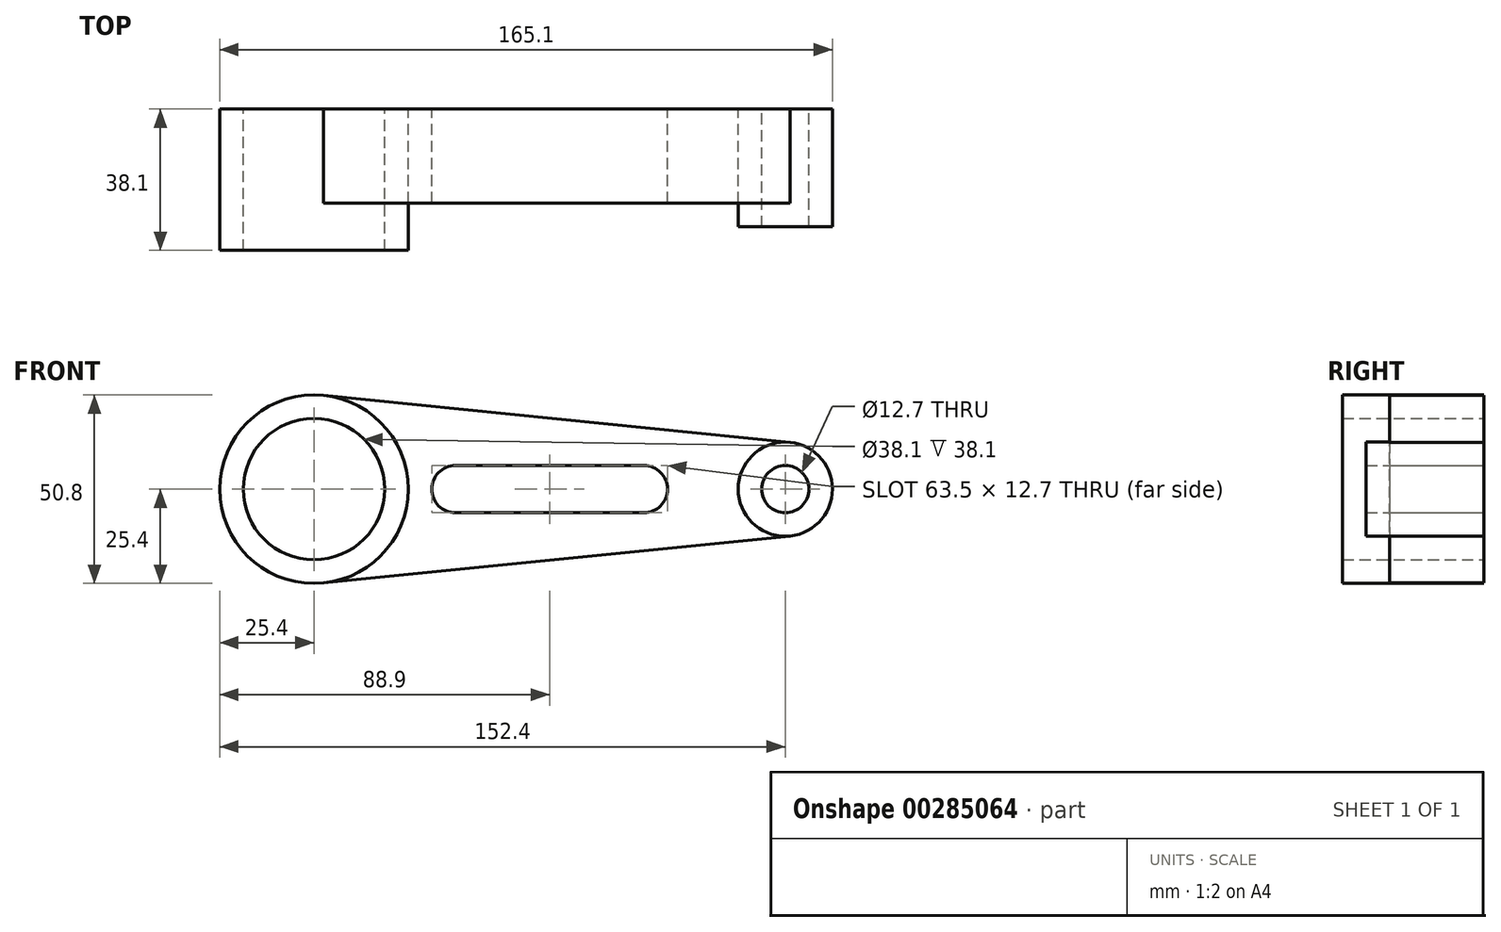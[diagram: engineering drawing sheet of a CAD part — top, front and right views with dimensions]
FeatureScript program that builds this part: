
annotation { "Feature Type Name" : "Feature", "Feature Type Description" : "" }
export const myFeature = defineFeature(function(context is Context, id is Id, definition is map)
    precondition{}
    {
        {
            var Q0;
            Q0=qCreatedBy(makeId("Front.planeOp"),FACE);
            var sketch = newSketch(context, id + "F0", { "sketchPlane" : qUnion([Q0])});
            skCircle(sketch, "E0", {"center": v(0, 0) * mm, "radius": 19.05 * mm});
            skCircle(sketch, "E1", {"center": v(0, 0) * mm, "radius": 25.4 * mm});
            skCircle(sketch, "E2", {"center": v(127, 0) * mm, "radius": 6.35 * mm});
            skCircle(sketch, "E3", {"center": v(127, 0) * mm, "radius": 12.7 * mm});
            skLineSegment(sketch, "E4", {"start": v(2.54, -25.27) * mm, "end": v(128.27, -12.64) * mm});
            skLineSegment(sketch, "E5", {"start": v(2.54, 25.27) * mm, "end": v(128.27, 12.64) * mm});
            skArc(sketch, "E6", {"start": v(88.9, -6.35) * mm, "mid": v(95.25, 0) * mm, "end": v(88.9, 6.35) * mm});
            skArc(sketch, "E7", {"start": v(38.1, 6.35) * mm, "mid": v(31.75, 0) * mm, "end": v(38.1, -6.35) * mm});
            skLineSegment(sketch, "E8", {"start": v(38.1, -6.35) * mm, "end": v(88.9, -6.35) * mm});
            skLineSegment(sketch, "E9", {"start": v(38.1, 6.35) * mm, "end": v(88.9, 6.35) * mm});
            skSolve(sketch);
        }
        {
            var Q0;
            Q0=makeQuery(id+"F0.imprint","IMPRINT",FACE,{"disambiguationData":[TD([[makeQuery(id+"F0.imprint","IMPRINT",EDGE,{"derivedFrom":sQuery(id+"F0.wireOp",EDGE,"E0")}),-1.0]])]});
            extrude(context, id + "F1", {"entities" : qUnion([Q0]), "depth" : 38.1 * mm});
        }
        {
            var Q0;
            {var subQ0=sQuery(id+"F0.wireOp",EDGE,"E4");Q0=makeQuery(id+"F0.imprint","IMPRINT",FACE,{"disambiguationData":[TD([[makeQuery(id+"F0.imprint","IMPRINT",EDGE,{"derivedFrom":subQ0}),1.0]])]});}
            extrude(context, id + "F2", {"entities" : qUnion([Q0]), "depth" : 25.4 * mm});
        }
        {
            var Q0;
            Q0=makeQuery(id+"F0.imprint","IMPRINT",FACE,{"disambiguationData":[TD([[makeQuery(id+"F0.imprint","IMPRINT",EDGE,{"derivedFrom":sQuery(id+"F0.wireOp",EDGE,"E2")}),-1.0]])]});
            extrude(context, id + "F3", {"entities" : qUnion([Q0]), "depth" : 31.75 * mm});
        }
    });
